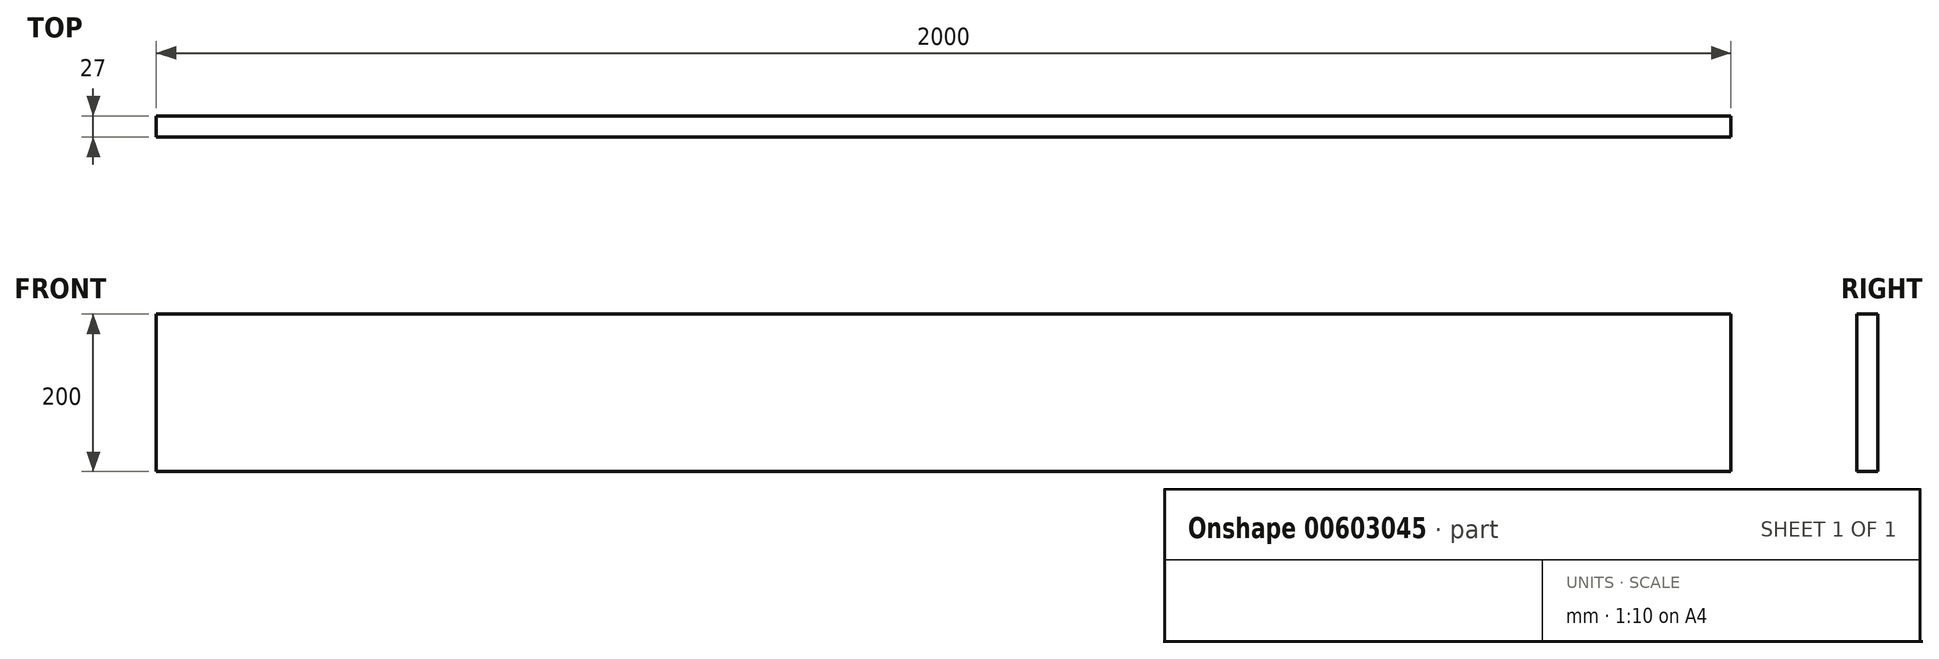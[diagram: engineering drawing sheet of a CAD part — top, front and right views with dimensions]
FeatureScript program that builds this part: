
annotation { "Feature Type Name" : "Feature", "Feature Type Description" : "" }
export const myFeature = defineFeature(function(context is Context, id is Id, definition is map)
    precondition{}
    {
        {
            var Q0;
            Q0=qCreatedBy(makeId("Front.planeOp"),FACE);
            var sketch = newSketch(context, id + "F0", { "sketchPlane" : qUnion([Q0])});
            skLineSegment(sketch, "E0.bottom", {"start": v(-501.36, 90.55) * mm, "end": v(1498.64, 90.55) * mm});
            skLineSegment(sketch, "E0.top", {"start": v(-501.36, -109.45) * mm, "end": v(1498.64, -109.45) * mm});
            skLineSegment(sketch, "E0.left", {"start": v(-501.36, 90.55) * mm, "end": v(-501.36, -109.45) * mm});
            skLineSegment(sketch, "E0.right", {"start": v(1498.64, 90.55) * mm, "end": v(1498.64, -109.45) * mm});
            skSolve(sketch);
        }
        {
            var Q0;
            Q0 = qSketchRegion(id + "F0", true);
            extrude(context, id + "F1", {"entities" : qUnion([Q0]), "depth" : 27 * mm, "offsetDistance" : 25 * mm});
        }
    });
